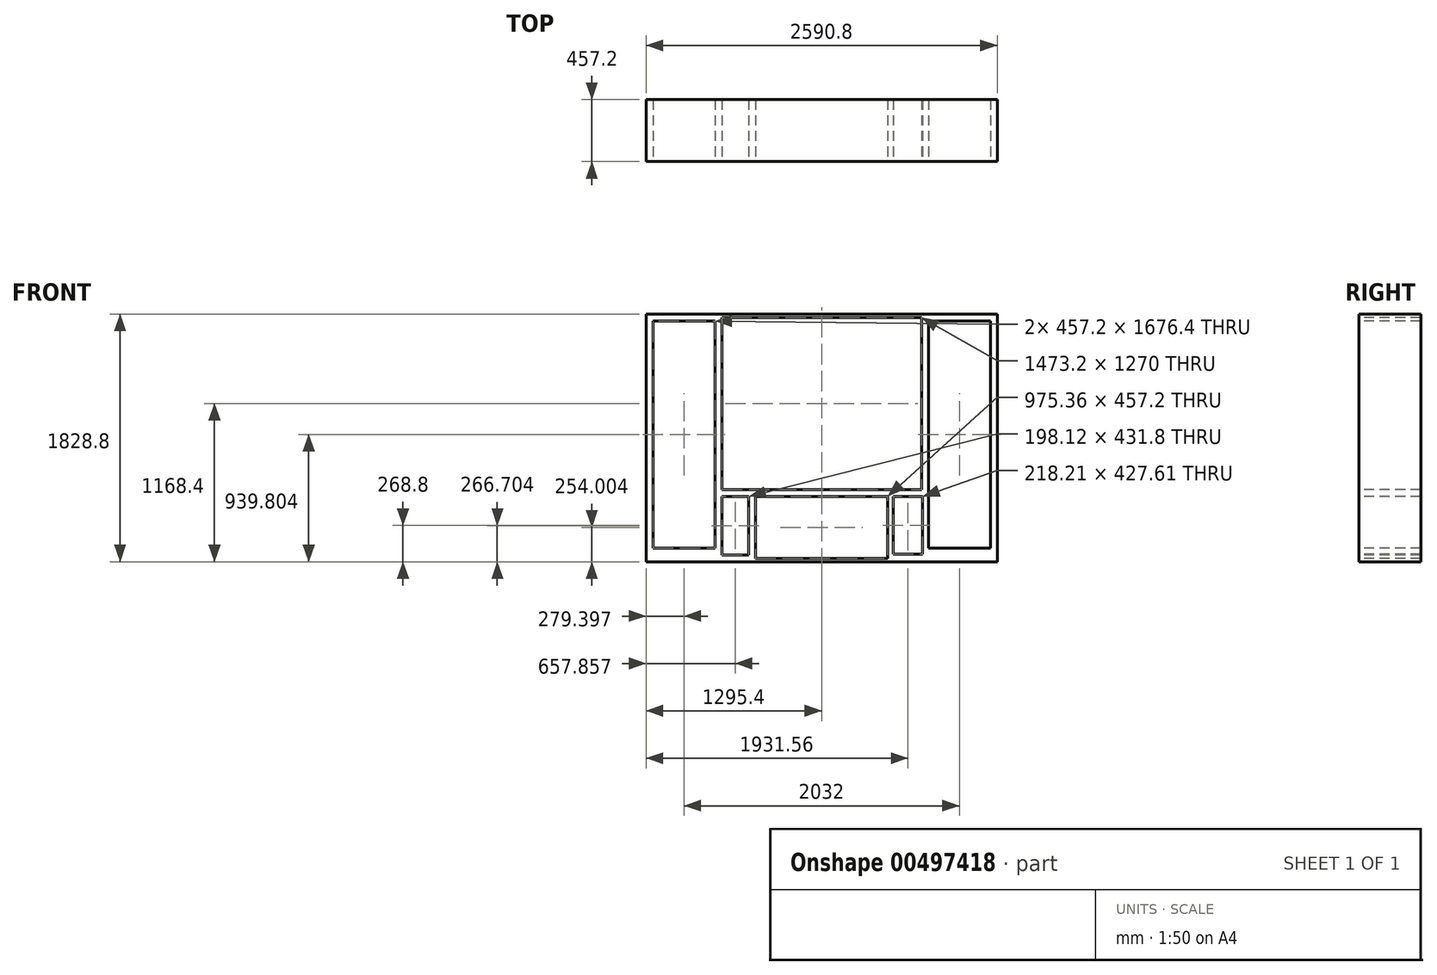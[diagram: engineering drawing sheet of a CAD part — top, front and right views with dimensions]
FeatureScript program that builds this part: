
annotation { "Feature Type Name" : "Feature", "Feature Type Description" : "" }
export const myFeature = defineFeature(function(context is Context, id is Id, definition is map)
    precondition{}
    {
        {
            var Q0;
            Q0=qCreatedBy(makeId("Front.planeOp"),FACE);
            var sketch = newSketch(context, id + "F0", { "sketchPlane" : qUnion([Q0])});
            skLineSegment(sketch, "E0.bottom", {"start": v(-758.22, 1021.48) * mm, "end": v(765.78, 1021.48) * mm});
            skLineSegment(sketch, "E0.top", {"start": v(-758.22, -807.32) * mm, "end": v(765.78, -807.32) * mm});
            skLineSegment(sketch, "E0.left", {"start": v(-758.22, 1021.48) * mm, "end": v(-758.22, -807.32) * mm});
            skLineSegment(sketch, "E0.right", {"start": v(765.78, 1021.48) * mm, "end": v(765.78, -807.32) * mm});
            skSolve(sketch);
        }
        {
            var Q0;
            Q0 = qSketchRegion(id + "F0", true);
            extrude(context, id + "F1", {"entities" : qUnion([Q0]), "depth" : 457.2 * mm});
        }
        {
            var Q0;
            Q0=makeQuery(id+"F1.opExtrude","CAP_FACE",FACE,{"disambiguationData":[OSD([sQuery(id+"F0.wireOp",EDGE,"E0.bottom"),sQuery(id+"F0.wireOp",EDGE,"E0.top"),sQuery(id+"F0.wireOp",EDGE,"E0.left"),sQuery(id+"F0.wireOp",EDGE,"E0.right")])],"isStart":false});
            var sketch = newSketch(context, id + "F2", { "sketchPlane" : qUnion([Q0])});
            skLineSegment(sketch, "E1.bottom", {"start": v(-732.82, 996.08) * mm, "end": v(740.38, 996.08) * mm});
            skLineSegment(sketch, "E1.top", {"start": v(-732.82, -273.92) * mm, "end": v(740.38, -273.92) * mm});
            skLineSegment(sketch, "E1.left", {"start": v(-732.82, 996.08) * mm, "end": v(-732.82, -273.92) * mm});
            skLineSegment(sketch, "E1.right", {"start": v(740.38, 996.08) * mm, "end": v(740.38, -273.92) * mm});
            skSolve(sketch);
        }
        {
            var Q0;
            Q0 = qSketchRegion(id + "F2", true);
            extrude(context, id + "F3", {"entities" : qUnion([Q0]), "operationType" : NewBodyOperationType.REMOVE, "endBound" : BoundingType.THROUGH_ALL, "oppositeDirection" : true, "depth" : 25.4 * mm});
        }
        {
            var Q0;
            Q0=makeQuery(id+"F1.opExtrude","CAP_FACE",FACE,{"disambiguationData":[OSD([sQuery(id+"F0.wireOp",EDGE,"E0.bottom"),sQuery(id+"F0.wireOp",EDGE,"E0.top"),sQuery(id+"F0.wireOp",EDGE,"E0.left"),sQuery(id+"F0.wireOp",EDGE,"E0.right")])],"isStart":false});
            var sketch = newSketch(context, id + "F4", { "sketchPlane" : qUnion([Q0])});
            skLineSegment(sketch, "E2.bottom", {"start": v(-483.9, -324.72) * mm, "end": v(491.46, -324.72) * mm});
            skLineSegment(sketch, "E2.top", {"start": v(-483.9, -781.92) * mm, "end": v(491.46, -781.92) * mm});
            skLineSegment(sketch, "E2.left", {"start": v(-483.9, -324.72) * mm, "end": v(-483.9, -781.92) * mm});
            skLineSegment(sketch, "E2.right", {"start": v(491.46, -324.72) * mm, "end": v(491.46, -781.92) * mm});
            skSolve(sketch);
        }
        {
            var Q0;
            Q0 = qSketchRegion(id + "F4", true);
            extrude(context, id + "F5", {"entities" : qUnion([Q0]), "operationType" : NewBodyOperationType.REMOVE, "endBound" : BoundingType.THROUGH_ALL, "oppositeDirection" : true, "depth" : 25.4 * mm});
        }
        {
            var Q0;
            Q0=makeQuery(id+"F1.opExtrude","SWEPT_FACE",FACE,{"disambiguationData":[OSD([sQuery(id+"F0.wireOp",EDGE,"E0.right")])]});
            var sketch = newSketch(context, id + "F6", { "sketchPlane" : qUnion([Q0])});
            skLineSegment(sketch, "E3.bottom", {"start": v(-457.2, 1021.48) * mm, "end": v(0, 1021.48) * mm});
            skLineSegment(sketch, "E3.top", {"start": v(-457.2, -807.32) * mm, "end": v(0, -807.32) * mm});
            skLineSegment(sketch, "E3.left", {"start": v(-457.2, 1021.48) * mm, "end": v(-457.2, -807.32) * mm});
            skLineSegment(sketch, "E3.right", {"start": v(0, 1021.48) * mm, "end": v(0, -807.32) * mm});
            skSolve(sketch);
        }
        {
            var Q0;
            Q0 = qSketchRegion(id + "F6", true);
            extrude(context, id + "F7", {"entities" : qUnion([Q0]), "operationType" : NewBodyOperationType.ADD, "depth" : 533.4 * mm});
        }
        {
            var Q0;
            Q0=makeQuery(id+"F1.opExtrude","SWEPT_FACE",FACE,{"disambiguationData":[OSD([sQuery(id+"F0.wireOp",EDGE,"E0.left")])]});
            var sketch = newSketch(context, id + "F8", { "sketchPlane" : qUnion([Q0])});
            skLineSegment(sketch, "E4.bottom", {"start": v(0, 1021.48) * mm, "end": v(457.2, 1021.48) * mm});
            skLineSegment(sketch, "E4.top", {"start": v(0, -807.32) * mm, "end": v(457.2, -807.32) * mm});
            skLineSegment(sketch, "E4.left", {"start": v(0, 1021.48) * mm, "end": v(0, -807.32) * mm});
            skLineSegment(sketch, "E4.right", {"start": v(457.2, 1021.48) * mm, "end": v(457.2, -807.32) * mm});
            skSolve(sketch);
        }
        {
            var Q0;
            Q0 = qSketchRegion(id + "F8", true);
            extrude(context, id + "F9", {"entities" : qUnion([Q0]), "operationType" : NewBodyOperationType.ADD, "depth" : 533.4 * mm});
        }
        {
            var Q0;
            Q0=makeQuery(id+"F9.boolean.opBoolean","MERGE",FACE,{"derivedFrom":[makeQuery(id+"F7.boolean.opBoolean","MERGE",FACE,{"derivedFrom":[makeQuery(id+"F1.opExtrude","CAP_FACE",FACE,{"disambiguationData":[OSD([sQuery(id+"F0.wireOp",EDGE,"E0.bottom"),sQuery(id+"F0.wireOp",EDGE,"E0.top"),sQuery(id+"F0.wireOp",EDGE,"E0.left"),sQuery(id+"F0.wireOp",EDGE,"E0.right")])],"isStart":false}),makeQuery(id+"F7.opExtrude","SWEPT_FACE",FACE,{"disambiguationData":[OSD([sQuery(id+"F6.wireOp",EDGE,"E3.left")])]})]}),makeQuery(id+"F9.opExtrude","SWEPT_FACE",FACE,{"disambiguationData":[OSD([sQuery(id+"F8.wireOp",EDGE,"E4.right")])]})]});
            var sketch = newSketch(context, id + "F10", { "sketchPlane" : qUnion([Q0])});
            skLineSegment(sketch, "E5.bottom", {"start": v(-1240.82, 970.68) * mm, "end": v(-783.62, 970.68) * mm});
            skLineSegment(sketch, "E5.top", {"start": v(-1240.82, -705.72) * mm, "end": v(-783.62, -705.72) * mm});
            skLineSegment(sketch, "E5.left", {"start": v(-1240.82, 970.68) * mm, "end": v(-1240.82, -705.72) * mm});
            skLineSegment(sketch, "E5.right", {"start": v(-783.62, 970.68) * mm, "end": v(-783.62, -705.72) * mm});
            skSolve(sketch);
        }
        {
            var Q0;
            Q0 = qSketchRegion(id + "F10", true);
            extrude(context, id + "F11", {"entities" : qUnion([Q0]), "operationType" : NewBodyOperationType.REMOVE, "endBound" : BoundingType.THROUGH_ALL, "oppositeDirection" : true, "depth" : 25.4 * mm});
        }
        {
            var Q0;
            Q0=makeQuery(id+"F9.boolean.opBoolean","MERGE",FACE,{"derivedFrom":[makeQuery(id+"F7.boolean.opBoolean","MERGE",FACE,{"derivedFrom":[makeQuery(id+"F1.opExtrude","CAP_FACE",FACE,{"disambiguationData":[OSD([sQuery(id+"F0.wireOp",EDGE,"E0.bottom"),sQuery(id+"F0.wireOp",EDGE,"E0.top"),sQuery(id+"F0.wireOp",EDGE,"E0.left"),sQuery(id+"F0.wireOp",EDGE,"E0.right")])],"isStart":false}),makeQuery(id+"F7.opExtrude","SWEPT_FACE",FACE,{"disambiguationData":[OSD([sQuery(id+"F6.wireOp",EDGE,"E3.left")])]})]}),makeQuery(id+"F9.opExtrude","SWEPT_FACE",FACE,{"disambiguationData":[OSD([sQuery(id+"F8.wireOp",EDGE,"E4.right")])]})]});
            var sketch = newSketch(context, id + "F12", { "sketchPlane" : qUnion([Q0])});
            skLineSegment(sketch, "E6.bottom", {"start": v(791.18, 970.68) * mm, "end": v(1248.38, 970.68) * mm});
            skLineSegment(sketch, "E6.top", {"start": v(791.18, -705.72) * mm, "end": v(1248.38, -705.72) * mm});
            skLineSegment(sketch, "E6.left", {"start": v(791.18, 970.68) * mm, "end": v(791.18, -705.72) * mm});
            skLineSegment(sketch, "E6.right", {"start": v(1248.38, 970.68) * mm, "end": v(1248.38, -705.72) * mm});
            skSolve(sketch);
        }
        {
            var Q0;
            Q0=makeQuery(id+"F12.imprint","IMPRINT",FACE,{"disambiguationData":[TD([[makeQuery(id+"F12.imprint","IMPRINT",EDGE,{"derivedFrom":sQuery(id+"F12.wireOp",EDGE,"E6.bottom")}),-1.0]])]});
            extrude(context, id + "F13", {"entities" : qUnion([Q0]), "operationType" : NewBodyOperationType.REMOVE, "endBound" : BoundingType.THROUGH_ALL, "oppositeDirection" : true, "depth" : 25.4 * mm});
        }
        {
            var Q0;
            Q0=makeQuery(id+"F9.boolean.opBoolean","MERGE",FACE,{"derivedFrom":[makeQuery(id+"F7.boolean.opBoolean","MERGE",FACE,{"derivedFrom":[makeQuery(id+"F1.opExtrude","CAP_FACE",FACE,{"disambiguationData":[OSD([sQuery(id+"F0.wireOp",EDGE,"E0.bottom"),sQuery(id+"F0.wireOp",EDGE,"E0.top"),sQuery(id+"F0.wireOp",EDGE,"E0.left"),sQuery(id+"F0.wireOp",EDGE,"E0.right")])],"isStart":false}),makeQuery(id+"F7.opExtrude","SWEPT_FACE",FACE,{"disambiguationData":[OSD([sQuery(id+"F6.wireOp",EDGE,"E3.left")])]})]}),makeQuery(id+"F9.opExtrude","SWEPT_FACE",FACE,{"disambiguationData":[OSD([sQuery(id+"F8.wireOp",EDGE,"E4.right")])]})]});
            var sketch = newSketch(context, id + "F14", { "sketchPlane" : qUnion([Q0])});
            skLineSegment(sketch, "E7.bottom", {"start": v(-732.82, -324.72) * mm, "end": v(-534.7, -324.72) * mm});
            skLineSegment(sketch, "E7.top", {"start": v(-732.82, -756.52) * mm, "end": v(-534.7, -756.52) * mm});
            skLineSegment(sketch, "E7.left", {"start": v(-732.82, -324.72) * mm, "end": v(-732.82, -756.52) * mm});
            skLineSegment(sketch, "E7.right", {"start": v(-534.7, -324.72) * mm, "end": v(-534.7, -756.52) * mm});
            skSolve(sketch);
        }
        {
            var Q0;
            Q0 = qSketchRegion(id + "F14", true);
            extrude(context, id + "F15", {"entities" : qUnion([Q0]), "operationType" : NewBodyOperationType.REMOVE, "endBound" : BoundingType.THROUGH_ALL, "oppositeDirection" : true, "depth" : 25.4 * mm});
        }
        {
            var Q0;
            Q0=makeQuery(id+"F9.boolean.opBoolean","MERGE",FACE,{"derivedFrom":[makeQuery(id+"F7.boolean.opBoolean","MERGE",FACE,{"derivedFrom":[makeQuery(id+"F1.opExtrude","CAP_FACE",FACE,{"disambiguationData":[OSD([sQuery(id+"F0.wireOp",EDGE,"E0.bottom"),sQuery(id+"F0.wireOp",EDGE,"E0.top"),sQuery(id+"F0.wireOp",EDGE,"E0.left"),sQuery(id+"F0.wireOp",EDGE,"E0.right")])],"isStart":false}),makeQuery(id+"F7.opExtrude","SWEPT_FACE",FACE,{"disambiguationData":[OSD([sQuery(id+"F6.wireOp",EDGE,"E3.left")])]})]}),makeQuery(id+"F9.opExtrude","SWEPT_FACE",FACE,{"disambiguationData":[OSD([sQuery(id+"F8.wireOp",EDGE,"E4.right")])]})]});
            var sketch = newSketch(context, id + "F16", { "sketchPlane" : qUnion([Q0])});
            skLineSegment(sketch, "E8.bottom", {"start": v(530.84, -324.72) * mm, "end": v(749.04, -324.72) * mm});
            skLineSegment(sketch, "E8.top", {"start": v(530.84, -752.32) * mm, "end": v(749.04, -752.32) * mm});
            skLineSegment(sketch, "E8.left", {"start": v(530.84, -324.72) * mm, "end": v(530.84, -752.32) * mm});
            skLineSegment(sketch, "E8.right", {"start": v(749.04, -324.72) * mm, "end": v(749.04, -752.32) * mm});
            skSolve(sketch);
        }
        {
            var Q0;
            Q0 = qSketchRegion(id + "F16", true);
            extrude(context, id + "F17", {"entities" : qUnion([Q0]), "operationType" : NewBodyOperationType.REMOVE, "endBound" : BoundingType.THROUGH_ALL, "oppositeDirection" : true, "depth" : 25.4 * mm});
        }
    });
